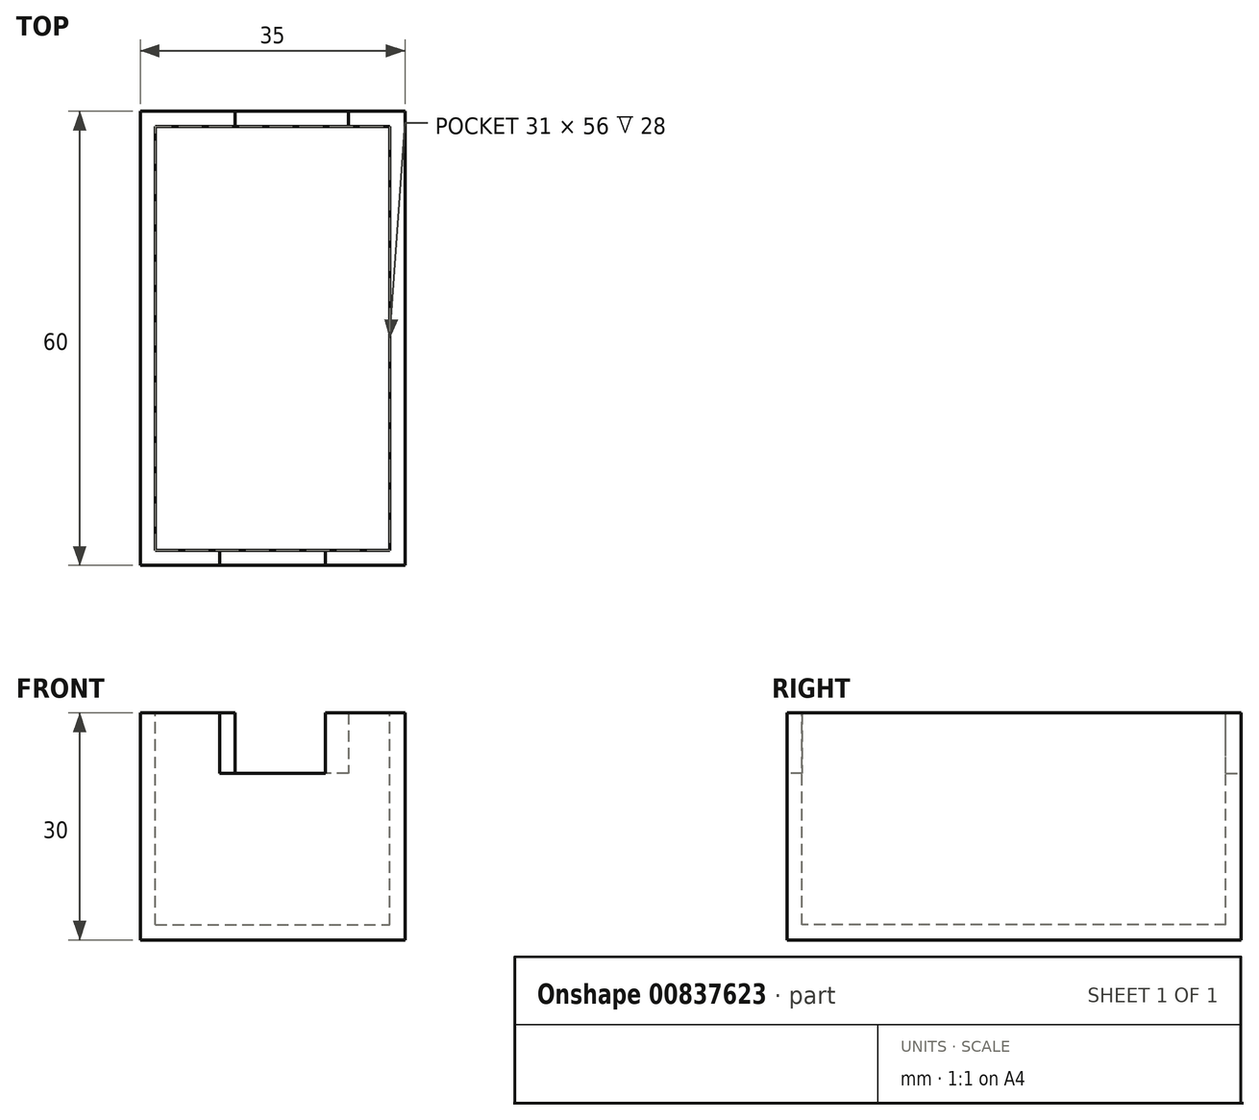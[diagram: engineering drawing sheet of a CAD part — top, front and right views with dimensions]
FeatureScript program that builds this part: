
annotation { "Feature Type Name" : "Feature", "Feature Type Description" : "" }
export const myFeature = defineFeature(function(context is Context, id is Id, definition is map)
    precondition{}
    {
        {
            var Q0;
            Q0=qCreatedBy(makeId("Top.planeOp"),FACE);
            var sketch = newSketch(context, id + "F0", { "sketchPlane" : qUnion([Q0])});
            skLineSegment(sketch, "E0.bottom", {"start": v(-17.5, 30) * mm, "end": v(17.5, 30) * mm});
            skLineSegment(sketch, "E0.top", {"start": v(-17.5, -30) * mm, "end": v(17.5, -30) * mm});
            skLineSegment(sketch, "E0.left", {"start": v(-17.5, 30) * mm, "end": v(-17.5, -30) * mm});
            skLineSegment(sketch, "E0.right", {"start": v(17.5, 30) * mm, "end": v(17.5, -30) * mm});
            skPoint(sketch, "E0.middle", {"position": v(0, 0) * mm});
            skSolve(sketch);
        }
        {
            var Q0;
            Q0=makeQuery(id+"F0.imprint","IMPRINT",FACE,{"disambiguationData":[TD([[makeQuery(id+"F0.imprint","IMPRINT",EDGE,{"derivedFrom":sQuery(id+"F0.wireOp",EDGE,"E0.bottom")}),-1.0]])]});
            extrude(context, id + "F1", {"entities" : qUnion([Q0]), "depth" : 30 * mm, "offsetDistance" : 25 * mm});
        }
        {
            var Q0;
            Q0=makeQuery(id+"F1.opExtrude","CAP_FACE",FACE,{"disambiguationData":[OSD([sQuery(id+"F0.wireOp",EDGE,"E0.bottom"),sQuery(id+"F0.wireOp",EDGE,"E0.top"),sQuery(id+"F0.wireOp",EDGE,"E0.left"),sQuery(id+"F0.wireOp",EDGE,"E0.right")])],"isStart":false});
            var sketch = newSketch(context, id + "F2", { "sketchPlane" : qUnion([Q0])});
            skLineSegment(sketch, "E1.bottom", {"start": v(-15.5, 28) * mm, "end": v(15.5, 28) * mm});
            skLineSegment(sketch, "E1.top", {"start": v(-15.5, -28) * mm, "end": v(15.5, -28) * mm});
            skLineSegment(sketch, "E1.left", {"start": v(-15.5, 28) * mm, "end": v(-15.5, -28) * mm});
            skLineSegment(sketch, "E1.right", {"start": v(15.5, 28) * mm, "end": v(15.5, -28) * mm});
            skPoint(sketch, "E1.middle", {"position": v(0, 0) * mm});
            skSolve(sketch);
        }
        {
            var Q0;
            Q0=makeQuery(id+"F2.imprint","IMPRINT",FACE,{"disambiguationData":[TD([[makeQuery(id+"F2.imprint","IMPRINT",EDGE,{"derivedFrom":sQuery(id+"F2.wireOp",EDGE,"E1.bottom")}),-1.0]])]});
            extrude(context, id + "F3", {"entities" : qUnion([Q0]), "operationType" : NewBodyOperationType.REMOVE, "oppositeDirection" : true, "depth" : 28 * mm, "offsetDistance" : 25 * mm});
        }
        {
            var Q0;
            Q0=makeQuery(id+"F1.opExtrude","SWEPT_FACE",FACE,{"disambiguationData":[OSD([sQuery(id+"F0.wireOp",EDGE,"E0.bottom")])]});
            var sketch = newSketch(context, id + "F4", { "sketchPlane" : qUnion([Q0])});
            skLineSegment(sketch, "E2.bottom", {"start": v(0, 30) * mm, "end": v(-10, 30) * mm});
            skLineSegment(sketch, "E2.top", {"start": v(0, 22) * mm, "end": v(-10, 22) * mm});
            skLineSegment(sketch, "E2.left", {"start": v(0, 30) * mm, "end": v(0, 22) * mm});
            skLineSegment(sketch, "E2.right", {"start": v(-10, 30) * mm, "end": v(-10, 22) * mm});
            skLineSegment(sketch, "E3.bottom", {"start": v(0, 22) * mm, "end": v(5, 22) * mm});
            skLineSegment(sketch, "E3.top", {"start": v(0, 30) * mm, "end": v(5, 30) * mm});
            skLineSegment(sketch, "E3.left", {"start": v(0, 22) * mm, "end": v(0, 30) * mm});
            skLineSegment(sketch, "E3.right", {"start": v(5, 22) * mm, "end": v(5, 30) * mm});
            skSolve(sketch);
        }
        {
            var Q0;
            Q0=makeQuery(id+"F4.imprint","IMPRINT",FACE,{"disambiguationData":[TD([[makeQuery(id+"F4.imprint","IMPRINT",EDGE,{"derivedFrom":sQuery(id+"F4.wireOp",EDGE,"E3.bottom")}),1.0]])]});
            var Q1;
            Q1=makeQuery(id+"F4.imprint","IMPRINT",FACE,{"disambiguationData":[TD([[makeQuery(id+"F4.imprint","IMPRINT",EDGE,{"derivedFrom":sQuery(id+"F4.wireOp",EDGE,"E2.bottom")}),1.0]])]});
            extrude(context, id + "F5", {"entities" : qUnion([Q0, Q1]), "operationType" : NewBodyOperationType.REMOVE, "oppositeDirection" : true, "depth" : 2 * mm, "offsetDistance" : 25 * mm});
        }
        {
            var Q0;
            Q0=makeQuery(id+"F1.opExtrude","SWEPT_FACE",FACE,{"disambiguationData":[OSD([sQuery(id+"F0.wireOp",EDGE,"E0.top")])]});
            var sketch = newSketch(context, id + "F6", { "sketchPlane" : qUnion([Q0])});
            skLineSegment(sketch, "E4.bottom", {"start": v(0, 30) * mm, "end": v(-7, 30) * mm});
            skLineSegment(sketch, "E4.top", {"start": v(0, 22) * mm, "end": v(-7, 22) * mm});
            skLineSegment(sketch, "E4.left", {"start": v(0, 30) * mm, "end": v(0, 22) * mm});
            skLineSegment(sketch, "E4.right", {"start": v(-7, 30) * mm, "end": v(-7, 22) * mm});
            skLineSegment(sketch, "E5.bottom", {"start": v(0, 30) * mm, "end": v(7, 30) * mm});
            skLineSegment(sketch, "E5.top", {"start": v(0, 22) * mm, "end": v(7, 22) * mm});
            skLineSegment(sketch, "E5.right", {"start": v(7, 30) * mm, "end": v(7, 22) * mm});
            skSolve(sketch);
        }
        {
            var Q0;
            Q0=makeQuery(id+"F6.imprint","IMPRINT",FACE,{"disambiguationData":[TD([[makeQuery(id+"F6.imprint","IMPRINT",EDGE,{"derivedFrom":sQuery(id+"F6.wireOp",EDGE,"E4.bottom")}),-1.0]])]});
            var Q1;
            Q1=makeQuery(id+"F6.imprint","IMPRINT",FACE,{"disambiguationData":[TD([[makeQuery(id+"F6.imprint","IMPRINT",EDGE,{"derivedFrom":sQuery(id+"F6.wireOp",EDGE,"E5.bottom")}),-1.0]])]});
            extrude(context, id + "F7", {"entities" : qUnion([Q0, Q1]), "operationType" : NewBodyOperationType.REMOVE, "oppositeDirection" : true, "depth" : 2 * mm, "offsetDistance" : 25 * mm});
        }
    });
